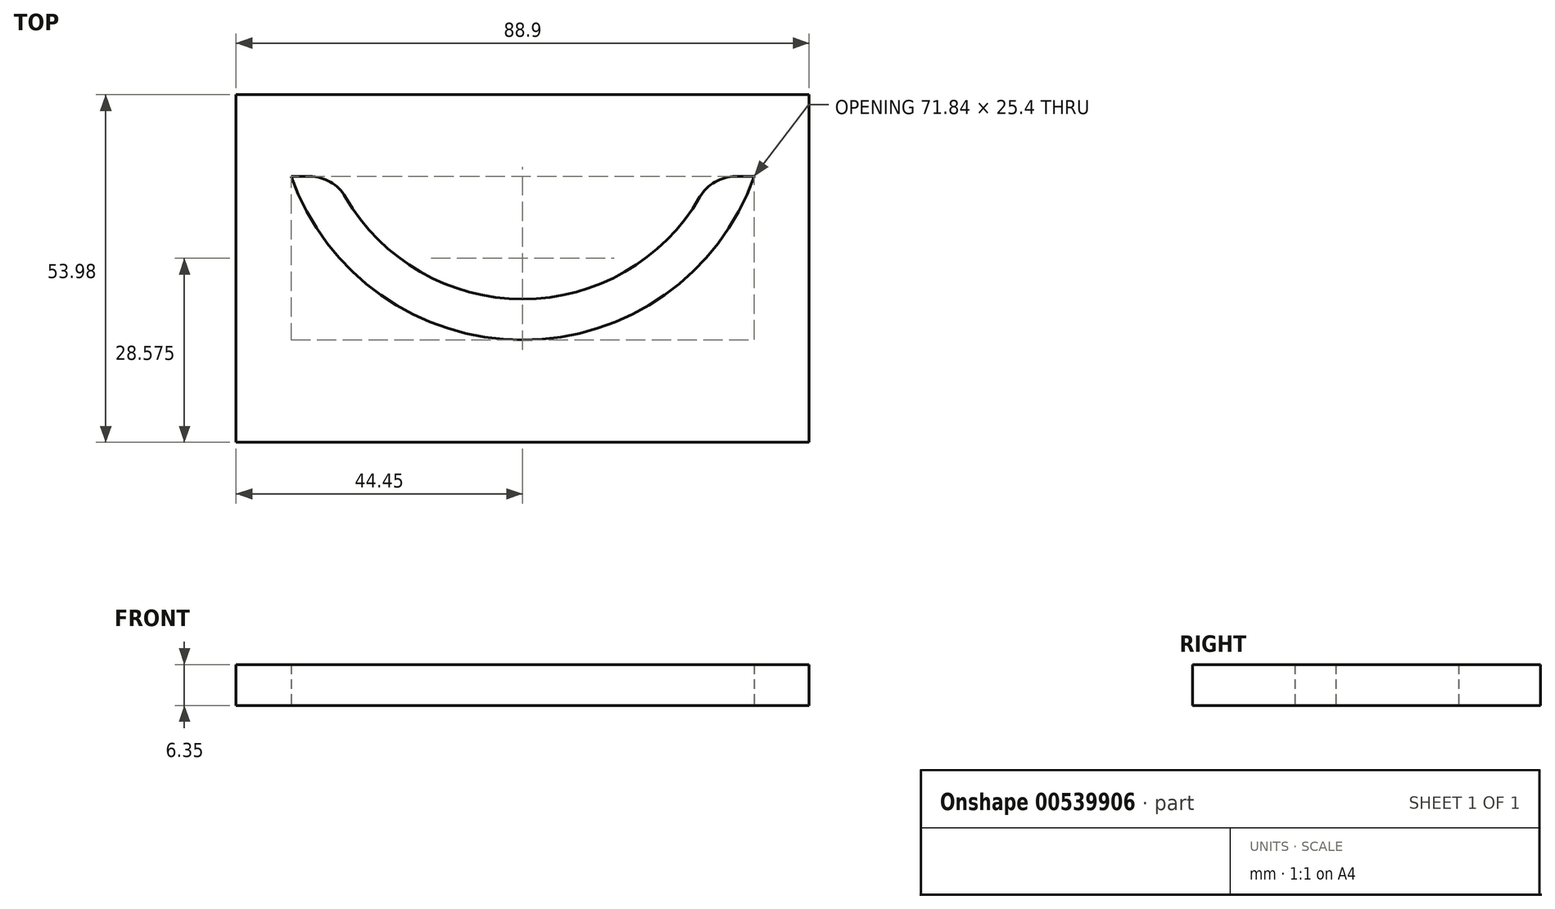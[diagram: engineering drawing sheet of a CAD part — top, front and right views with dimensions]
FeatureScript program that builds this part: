
annotation { "Feature Type Name" : "Feature", "Feature Type Description" : "" }
export const myFeature = defineFeature(function(context is Context, id is Id, definition is map)
    precondition{}
    {
        {
            var Q0;
            Q0=qCreatedBy(makeId("Top.planeOp"),FACE);
            var sketch = newSketch(context, id + "F0", { "sketchPlane" : qUnion([Q0])});
            skLineSegment(sketch, "E0.bottom", {"start": v(-88.9, 53.97) * mm, "end": v(0, 53.97) * mm});
            skLineSegment(sketch, "E0.top", {"start": v(-88.9, 0) * mm, "end": v(0, 0) * mm});
            skLineSegment(sketch, "E0.left", {"start": v(-88.9, 53.98) * mm, "end": v(-88.9, 0) * mm});
            skLineSegment(sketch, "E0.right", {"start": v(0, 53.97) * mm, "end": v(0, 0) * mm});
            skPoint(sketch, "E1", {"position": v(-44.45, 53.97) * mm});
            skArc(sketch, "E2", {"start": v(-71.95, 38.1) * mm, "mid": v(-44.45, 22.22) * mm, "end": v(-16.95, 38.1) * mm});
            skArc(sketch, "E3.0", {"start": v(-80.37, 41.27) * mm, "mid": v(-44.45, 15.87) * mm, "end": v(-8.53, 41.27) * mm});
            skLineSegment(sketch, "E4", {"start": v(-44.45, 53.97) * mm, "end": v(-44.45, 41.27) * mm, "construction": true});
            skLineSegment(sketch, "E5", {"start": v(-77.45, 41.27) * mm, "end": v(-80.37, 41.27) * mm});
            skLineSegment(sketch, "E6", {"start": v(-11.45, 41.27) * mm, "end": v(-8.53, 41.27) * mm});
            skPoint(sketch, "E7.visualSharp", {"position": v(-73.55, 41.27) * mm});
            skArc(sketch, "E7.filletArc", {"start": v(-71.95, 38.1) * mm, "mid": v(-74.27, 40.42) * mm, "end": v(-77.45, 41.27) * mm});
            skPoint(sketch, "E8.visualSharp", {"position": v(-15.35, 41.27) * mm});
            skArc(sketch, "E8.filletArc", {"start": v(-11.45, 41.27) * mm, "mid": v(-14.63, 40.42) * mm, "end": v(-16.95, 38.1) * mm});
            skSolve(sketch);
        }
        {
            var Q0;
            Q0 = qSketchRegion(id + "F0", true);
            extrude(context, id + "F1", {"entities" : qUnion([Q0]), "depth" : 6.35 * mm, "offsetDistance" : 25.4 * mm});
        }
    });
